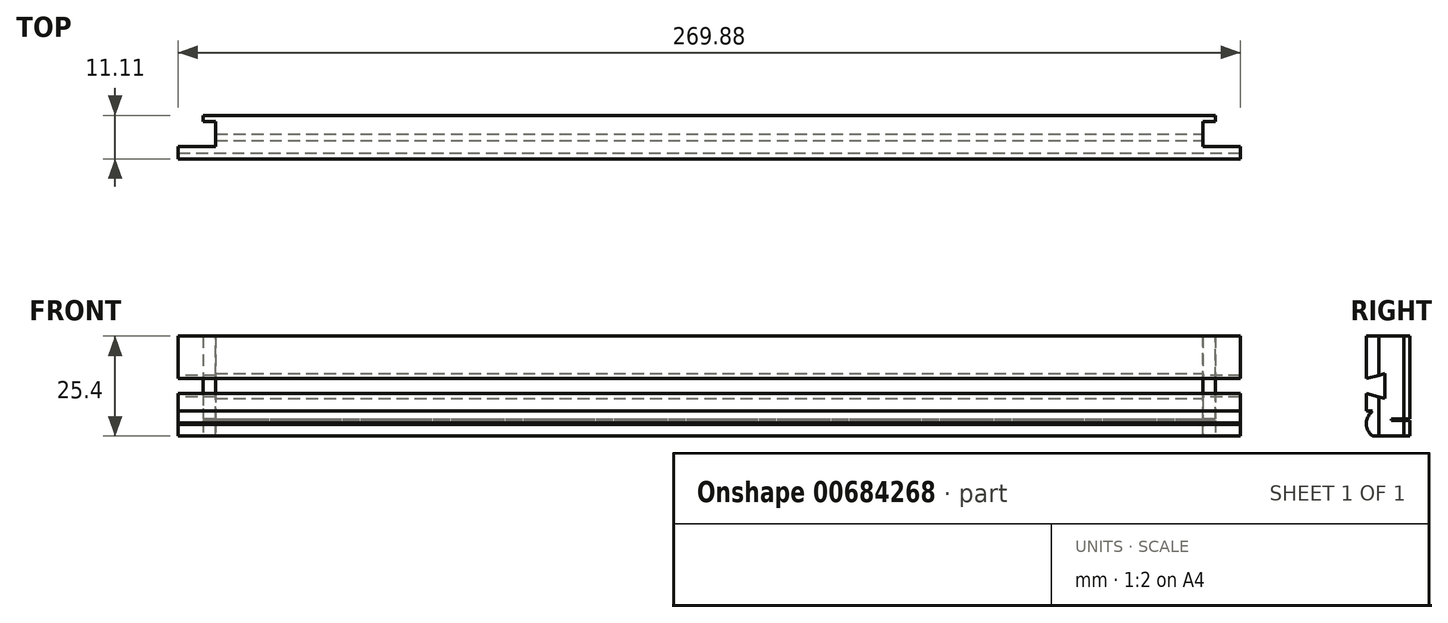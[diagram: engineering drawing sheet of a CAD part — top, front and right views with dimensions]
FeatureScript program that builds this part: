
annotation { "Feature Type Name" : "Feature", "Feature Type Description" : "" }
export const myFeature = defineFeature(function(context is Context, id is Id, definition is map)
    precondition{}
    {
        {
            var Q0;
            Q0=qCreatedBy(makeId("Top.planeOp"),FACE);
            var sketch = newSketch(context, id + "F0", { "sketchPlane" : qUnion([Q0])});
            skLineSegment(sketch, "E0", {"start": v(-134.94, 0) * mm, "end": v(134.94, 0) * mm});
            skLineSegment(sketch, "E1", {"start": v(134.94, 0) * mm, "end": v(134.94, -11.11) * mm});
            skLineSegment(sketch, "E2", {"start": v(134.94, -11.11) * mm, "end": v(-134.94, -11.11) * mm});
            skLineSegment(sketch, "E3", {"start": v(-134.94, -11.11) * mm, "end": v(-134.94, 0) * mm});
            skLineSegment(sketch, "E4", {"start": v(0, 0) * mm, "end": v(0, -70.04) * mm, "construction": true});
            skSolve(sketch);
        }
        {
            var Q0;
            Q0=makeQuery(id+"F0.imprint","IMPRINT",FACE,{"disambiguationData":[TD([[makeQuery(id+"F0.imprint","IMPRINT",EDGE,{"derivedFrom":sQuery(id+"F0.wireOp",EDGE,"E0")}),-1.0]])]});
            extrude(context, id + "F1", {"entities" : qUnion([Q0]), "depth" : 25.4 * mm, "offsetDistance" : 25.4 * mm});
        }
        {
            var Q0;
            Q0=makeQuery(id+"F1.opExtrude","SWEPT_FACE",FACE,{"disambiguationData":[OSD([sQuery(id+"F0.wireOp",EDGE,"E1")])]});
            var sketch = newSketch(context, id + "F2", { "sketchPlane" : qUnion([Q0])});
            skLineSegment(sketch, "E5", {"start": v(-11.11, 25.4) * mm, "end": v(-7.94, 25.4) * mm});
            skLineSegment(sketch, "E6", {"start": v(-7.94, 25.4) * mm, "end": v(-7.94, 0) * mm});
            skLineSegment(sketch, "E7", {"start": v(-7.94, 0) * mm, "end": v(-1.59, 0) * mm});
            skLineSegment(sketch, "E8", {"start": v(-1.59, 0) * mm, "end": v(-1.59, 25.4) * mm});
            skSolve(sketch);
        }
        {
            var Q0;
            {var subQ0=sQuery(id+"F2.wireOp",EDGE,"E6");Q0=makeQuery(id+"F2.imprint","IMPRINT",FACE,{"disambiguationData":[TD([[makeQuery(id+"F2.imprint","IMPRINT",EDGE,{"derivedFrom":subQ0}),1.0]])]});}
            extrude(context, id + "F3", {"entities" : qUnion([Q0]), "operationType" : NewBodyOperationType.REMOVE, "oppositeDirection" : true, "depth" : 9.52 * mm, "offsetDistance" : 25.4 * mm});
        }
        {
            var Q0;
            {var subQ0=sQuery(id+"F0.wireOp",EDGE,"E0");var subQ3=sQuery(id+"F0.wireOp",EDGE,"E1");Q0=makeQuery(id+"F3.boolean.opBoolean","SPLIT",FACE,{"disambiguationData":[TD([makeQuery(id+"F1.opExtrude","SWEPT_FACE",FACE,{"disambiguationData":[OSD([subQ0])]})])],"derivedFrom":makeQuery(id+"F1.opExtrude","SWEPT_FACE",FACE,{"disambiguationData":[OSD([subQ3])]})});}
            extrude(context, id + "F4", {"entities" : qUnion([Q0]), "operationType" : NewBodyOperationType.REMOVE, "oppositeDirection" : true, "depth" : 6.35 * mm, "offsetDistance" : 25.4 * mm});
        }
        {
            var Q0;
            Q0=makeQuery(id+"F1.opExtrude","SWEPT_FACE",FACE,{"disambiguationData":[OSD([sQuery(id+"F0.wireOp",EDGE,"E3")])]});
            var sketch = newSketch(context, id + "F5", { "sketchPlane" : qUnion([Q0])});
            skLineSegment(sketch, "E9", {"start": v(7.94, 0) * mm, "end": v(7.94, 25.4) * mm});
            skLineSegment(sketch, "E10", {"start": v(7.94, 25.4) * mm, "end": v(1.59, 25.4) * mm});
            skLineSegment(sketch, "E11", {"start": v(1.59, 25.4) * mm, "end": v(1.59, 0) * mm});
            skLineSegment(sketch, "E12", {"start": v(1.59, 0) * mm, "end": v(0, 0) * mm});
            skSolve(sketch);
        }
        {
            var Q0;
            {var subQ0=sQuery(id+"F5.wireOp",EDGE,"E11");Q0=makeQuery(id+"F5.imprint","IMPRINT",FACE,{"disambiguationData":[TD([[makeQuery(id+"F5.imprint","IMPRINT",EDGE,{"derivedFrom":subQ0}),-1.0]])]});}
            extrude(context, id + "F6", {"entities" : qUnion([Q0]), "operationType" : NewBodyOperationType.REMOVE, "oppositeDirection" : true, "depth" : 6.35 * mm, "offsetDistance" : 25.4 * mm});
        }
        {
            var Q0;
            {var subQ0=sQuery(id+"F5.wireOp",EDGE,"E9");Q0=makeQuery(id+"F5.imprint","IMPRINT",FACE,{"disambiguationData":[TD([[makeQuery(id+"F5.imprint","IMPRINT",EDGE,{"derivedFrom":subQ0}),1.0]])]});}
            extrude(context, id + "F7", {"entities" : qUnion([Q0]), "operationType" : NewBodyOperationType.REMOVE, "oppositeDirection" : true, "depth" : 9.52 * mm, "offsetDistance" : 25.4 * mm});
        }
        {
            var Q0;
            Q0=makeQuery(id+"F2.imprint","IMPRINT",FACE,{"disambiguationData":[TD([[makeQuery(id+"F2.imprint","IMPRINT",EDGE,{"derivedFrom":sQuery(id+"F2.wireOp",EDGE,"E5")}),1.0]])]});
            var sketch = newSketch(context, id + "F8", { "sketchPlane" : qUnion([Q0])});
            skLineSegment(sketch, "E13", {"start": v(0, 3.97) * mm, "end": v(-4.76, 3.97) * mm});
            skLineSegment(sketch, "E14", {"start": v(-4.76, 3.97) * mm, "end": v(-4.76, 4.37) * mm});
            skLineSegment(sketch, "E15", {"start": v(-4.76, 4.37) * mm, "end": v(0, 4.37) * mm});
            skLineSegment(sketch, "E16", {"start": v(0, 4.37) * mm, "end": v(0, 3.97) * mm});
            skSolve(sketch);
        }
        {
            var Q0;
            Q0=makeQuery(id+"F8.imprint","IMPRINT",FACE,{"disambiguationData":[TD([[makeQuery(id+"F8.imprint","IMPRINT",EDGE,{"derivedFrom":sQuery(id+"F8.wireOp",EDGE,"E13")}),-1.0]])]});
            extrude(context, id + "F9", {"entities" : qUnion([Q0]), "operationType" : NewBodyOperationType.REMOVE, "endBound" : BoundingType.THROUGH_ALL, "oppositeDirection" : true, "depth" : 25.4 * mm, "offsetDistance" : 25.4 * mm});
        }
        {
            var Q0;
            Q0=makeQuery(id+"F2.imprint","IMPRINT",FACE,{"disambiguationData":[TD([[makeQuery(id+"F2.imprint","IMPRINT",EDGE,{"derivedFrom":sQuery(id+"F2.wireOp",EDGE,"E5")}),1.0]])]});
            var sketch = newSketch(context, id + "F10", { "sketchPlane" : qUnion([Q0])});
            skLineSegment(sketch, "E17", {"start": v(-9.53, 0) * mm, "end": v(-9.53, 6.35) * mm, "construction": true});
            skLineSegment(sketch, "E18", {"start": v(-9.53, 6.35) * mm, "end": v(-11.12, 6.35) * mm});
            skLineSegment(sketch, "E19", {"start": v(-9.53, 3.18) * mm, "end": v(-11.12, 3.18) * mm, "construction": true});
            skArc(sketch, "E20", {"start": v(-9.53, 6.35) * mm, "mid": v(-11.12, 3.17) * mm, "end": v(-9.53, 0) * mm});
            skLineSegment(sketch, "E21", {"start": v(-11.12, 0) * mm, "end": v(-11.12, 12.7) * mm});
            skLineSegment(sketch, "E22", {"start": v(-11.12, 12.7) * mm, "end": v(-6.36, 12.7) * mm});
            skLineSegment(sketch, "E23.MirrorCS", {"start": v(-6.36, 9.53) * mm, "end": v(-11.12, 10.8) * mm});
            skLineSegment(sketch, "E24.MirrorCS", {"start": v(-6.36, 15.88) * mm, "end": v(-11.12, 14.6) * mm});
            skLineSegment(sketch, "E25", {"start": v(-6.36, 15.88) * mm, "end": v(-6.36, 9.53) * mm});
            skSolve(sketch);
        }
        {
            var Q0;
            {var subQ0=sQuery(id+"F10.wireOp",EDGE,"E20");var subQ1=sQuery(id+"F0.wireOp",EDGE,"E1");var subQ3=makeQuery(id+"F1.opExtrude","SWEPT_EDGE",EDGE,{"disambiguationData":[OSD([subQ1,sQuery(id+"F0.wireOp",EDGE,"E2")])]});var subQ6=makeQuery(id+"F2.imprint","IMPRINT",EDGE,{"derivedFrom":subQ3});var subQ7=makeQuery(id+"F10.imprint","INTERSECT",VERTEX,{"disambiguationData":[OD(1.0)],"derivedFrom":[subQ6,subQ0]});Q0=makeQuery(id+"F10.imprint","IMPRINT",FACE,{"disambiguationData":[TD([[makeQuery(id+"F10.imprint","IMPRINT",EDGE,{"disambiguationData":[TD([[subQ7,-1.0]])],"derivedFrom":subQ0}),-1.0]])]});}
            var Q1;
            {var subQ0=sQuery(id+"F10.wireOp",EDGE,"E20");var subQ1=sQuery(id+"F0.wireOp",EDGE,"E1");var subQ3=makeQuery(id+"F1.opExtrude","SWEPT_EDGE",EDGE,{"disambiguationData":[OSD([subQ1,sQuery(id+"F0.wireOp",EDGE,"E2")])]});var subQ6=makeQuery(id+"F2.imprint","IMPRINT",EDGE,{"derivedFrom":subQ3});var subQ7=makeQuery(id+"F10.imprint","INTERSECT",VERTEX,{"disambiguationData":[OD(0.0)],"derivedFrom":[subQ6,subQ0]});Q1=makeQuery(id+"F10.imprint","IMPRINT",FACE,{"disambiguationData":[TD([[makeQuery(id+"F10.imprint","IMPRINT",EDGE,{"disambiguationData":[TD([[subQ7,-1.0]])],"derivedFrom":subQ0}),-1.0]])]});}
            extrude(context, id + "F11", {"entities" : qUnion([Q0, Q1]), "operationType" : NewBodyOperationType.REMOVE, "endBound" : BoundingType.THROUGH_ALL, "oppositeDirection" : true, "depth" : 25.4 * mm, "offsetDistance" : 25.4 * mm});
        }
        {
            var Q0;
            {var subQ0=sQuery(id+"F10.wireOp",EDGE,"E20");var subQ1=sQuery(id+"F10.wireOp",EDGE,"E18");var subQ2=makeQuery(id+"F10.imprint","INTERSECT",VERTEX,{"derivedFrom":[subQ1,subQ0]});Q0=makeQuery(id+"F10.imprint","IMPRINT",FACE,{"disambiguationData":[TD([[makeQuery(id+"F10.imprint","IMPRINT",EDGE,{"disambiguationData":[TD([[subQ2,-1.0]])],"derivedFrom":subQ1}),1.0]])]});}
            extrude(context, id + "F12", {"entities" : qUnion([Q0]), "operationType" : NewBodyOperationType.REMOVE, "endBound" : BoundingType.UP_TO_NEXT, "oppositeDirection" : true, "depth" : 513.84 * mm, "offsetDistance" : 25.4 * mm});
        }
        {
            var Q0;
            {var subQ3=makeQuery(id+"F2.imprint","IMPRINT",EDGE,{"derivedFrom":sQuery(id+"F2.wireOp",EDGE,"E6")});var subQ5=sQuery(id+"F10.wireOp",EDGE,"E24.MirrorCS");var subQ7=makeQuery(id+"F10.imprint","INTERSECT",VERTEX,{"derivedFrom":[subQ3,subQ5]});Q0=makeQuery(id+"F10.imprint","IMPRINT",FACE,{"disambiguationData":[TD([[makeQuery(id+"F10.imprint","IMPRINT",EDGE,{"disambiguationData":[TD([[subQ7,-1.0]])],"derivedFrom":subQ3}),-1.0]])]});}
            var Q1;
            {var subQ0=sQuery(id+"F10.wireOp",EDGE,"E25");var subQ1=sQuery(id+"F10.wireOp",EDGE,"E22");var subQ2=makeQuery(id+"F10.imprint","INTERSECT",VERTEX,{"derivedFrom":[subQ1,subQ0]});Q1=makeQuery(id+"F10.imprint","IMPRINT",FACE,{"disambiguationData":[TD([[makeQuery(id+"F10.imprint","IMPRINT",EDGE,{"disambiguationData":[TD([[subQ2,1.0]])],"derivedFrom":subQ1}),1.0]])]});}
            var Q2;
            {var subQ0=sQuery(id+"F10.wireOp",EDGE,"E25");var subQ1=sQuery(id+"F10.wireOp",EDGE,"E22");var subQ2=makeQuery(id+"F10.imprint","INTERSECT",VERTEX,{"derivedFrom":[subQ1,subQ0]});Q2=makeQuery(id+"F10.imprint","IMPRINT",FACE,{"disambiguationData":[TD([[makeQuery(id+"F10.imprint","IMPRINT",EDGE,{"disambiguationData":[TD([[subQ2,1.0]])],"derivedFrom":subQ1}),-1.0]])]});}
            var Q3;
            {var subQ3=makeQuery(id+"F2.imprint","IMPRINT",EDGE,{"derivedFrom":sQuery(id+"F2.wireOp",EDGE,"E6")});var subQ5=sQuery(id+"F10.wireOp",EDGE,"E23.MirrorCS");var subQ7=makeQuery(id+"F10.imprint","INTERSECT",VERTEX,{"derivedFrom":[subQ3,subQ5]});Q3=makeQuery(id+"F10.imprint","IMPRINT",FACE,{"disambiguationData":[TD([[makeQuery(id+"F10.imprint","IMPRINT",EDGE,{"disambiguationData":[TD([[subQ7,1.0]])],"derivedFrom":subQ3}),-1.0]])]});}
            extrude(context, id + "F13", {"entities" : qUnion([Q0, Q1, Q2, Q3]), "operationType" : NewBodyOperationType.REMOVE, "endBound" : BoundingType.THROUGH_ALL, "oppositeDirection" : true, "depth" : 25.4 * mm, "offsetDistance" : 25.4 * mm});
        }
    });
